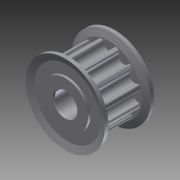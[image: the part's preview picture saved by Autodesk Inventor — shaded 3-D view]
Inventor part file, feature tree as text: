
AUTODESK INVENTOR PART (.ipt)
format: ipt  version: 2012 (Build 160160000, 160)  size: 253,952 bytes
history: native  units: in
note: dims shown in document units (in); Inventor stores cm internally (conversion verified against a paired STEP export)
features: extrude x2, sketch x1, chamfer x1, imported_body x1
ambient origin geometry x8: Origin, YZ Plane, XZ Plane, XY Plane, X Axis, Y Axis, Z Axis, Center Point
feature tree (5):
  sketch  "Sketch1"  dims[d0=0.25in d1=0.3937in d2=0.0in d3=0.248in d4=0.0in d7=0.0098in d8=0.0787in d9=45.0deg]
  extrude  "Extrusion1"  Depth=0.3937in TaperAngle=0.0deg
  extrude  "Extrusion2"  Depth=0.248in TaperAngle=0.0deg
  chamfer  "Chamfer1"  Distance=0.0098in Angle=45.0deg
  imported_body  "Base1"
